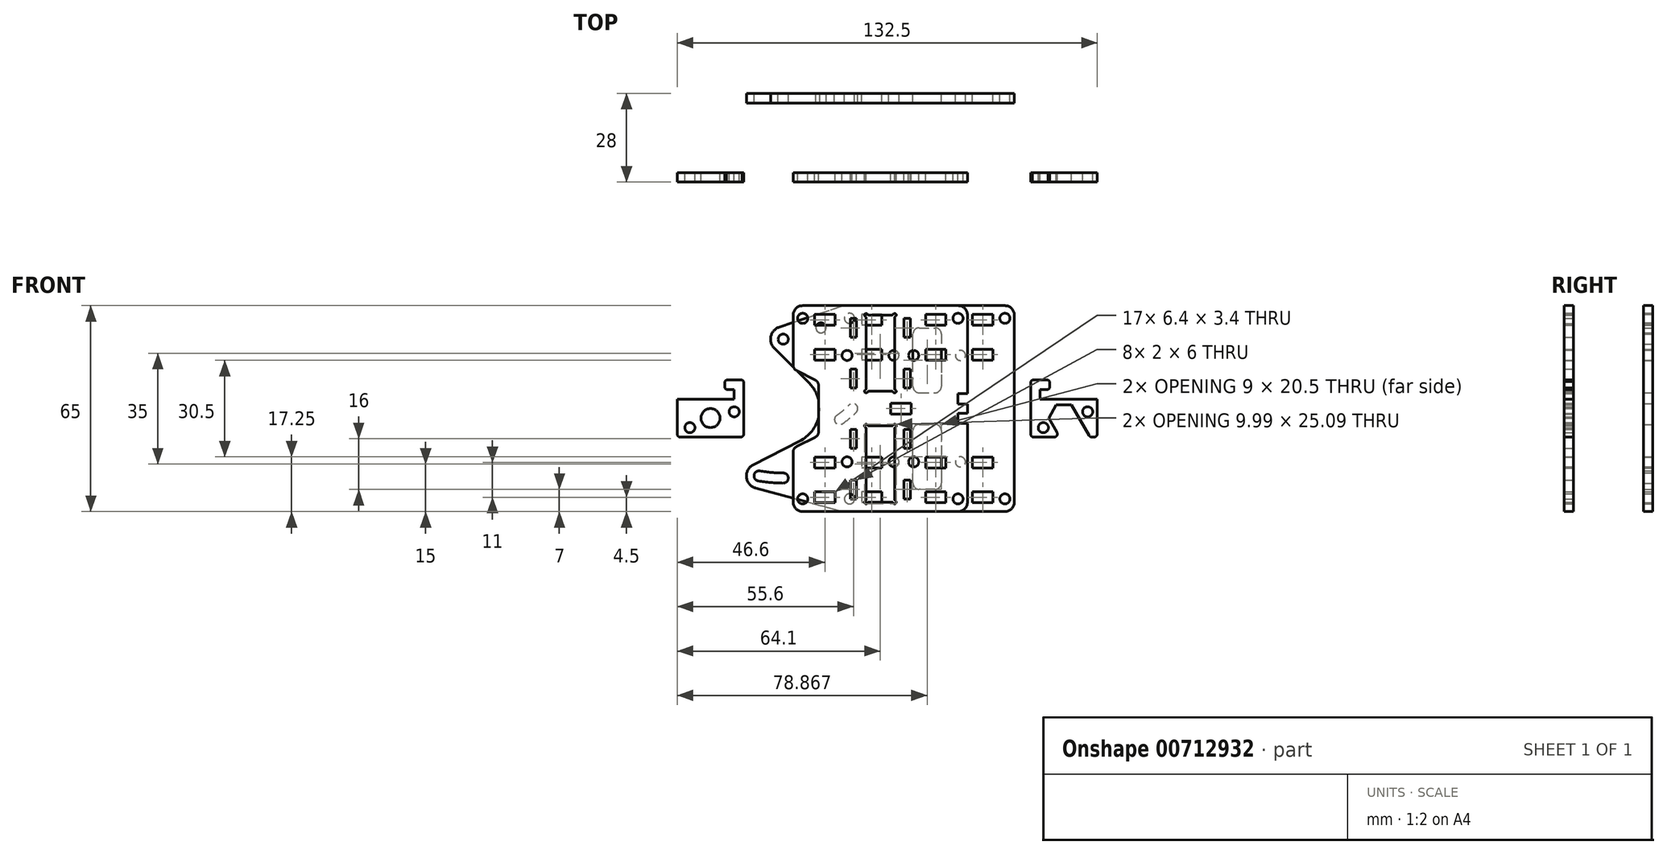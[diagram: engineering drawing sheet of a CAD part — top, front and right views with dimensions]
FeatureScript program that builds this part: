
annotation { "Feature Type Name" : "Feature", "Feature Type Description" : "" }
export const myFeature = defineFeature(function(context is Context, id is Id, definition is map)
    precondition{}
    {
        {
            var Q0;
            Q0=qCreatedBy(makeId("Front.planeOp"),FACE);
            var sketch = newSketch(context, id + "F0", { "sketchPlane" : qUnion([Q0])});
            skLineSegment(sketch, "E0", {"start": v(-7.5, 12.5) * mm, "end": v(-9.5, 12.5) * mm});
            skLineSegment(sketch, "E1", {"start": v(9.5, 12.5) * mm, "end": v(7.5, 12.5) * mm});
            skLineSegment(sketch, "E2", {"start": v(-9.5, -12.5) * mm, "end": v(-7.5, -12.5) * mm});
            skLineSegment(sketch, "E3", {"start": v(7.5, -12.5) * mm, "end": v(9.5, -12.5) * mm});
            skLineSegment(sketch, "E4", {"start": v(-7.5, -22.5) * mm, "end": v(-9.5, -22.5) * mm});
            skLineSegment(sketch, "E5", {"start": v(9.5, -22.5) * mm, "end": v(7.5, -22.5) * mm});
            skLineSegment(sketch, "E6", {"start": v(-9.5, 22.5) * mm, "end": v(-7.5, 22.5) * mm});
            skLineSegment(sketch, "E7", {"start": v(7.5, 22.5) * mm, "end": v(9.5, 22.5) * mm});
            skLineSegment(sketch, "E8", {"start": v(27.5, 1.5) * mm, "end": v(27.5, -1.5) * mm});
            skArc(sketch, "E9", {"start": v(4.75, 29.12) * mm, "mid": v(4.85, 29.9) * mm, "end": v(4.07, 29.8) * mm});
            skArc(sketch, "E10", {"start": v(3.63, 29.55) * mm, "mid": v(3.88, 29.62) * mm, "end": v(4.07, 29.8) * mm});
            skArc(sketch, "E11", {"start": v(4.75, 29.12) * mm, "mid": v(4.57, 28.93) * mm, "end": v(4.5, 28.68) * mm});
            skLineSegment(sketch, "E12", {"start": v(4.5, 6.32) * mm, "end": v(4.5, 28.68) * mm});
            skArc(sketch, "E13", {"start": v(4.5, 6.32) * mm, "mid": v(4.57, 6.07) * mm, "end": v(4.75, 5.88) * mm});
            skArc(sketch, "E14", {"start": v(4.07, 5.2) * mm, "mid": v(4.85, 5.1) * mm, "end": v(4.75, 5.88) * mm});
            skArc(sketch, "E15", {"start": v(4.07, 5.2) * mm, "mid": v(3.88, 5.38) * mm, "end": v(3.63, 5.45) * mm});
            skLineSegment(sketch, "E16", {"start": v(-3.63, 5.45) * mm, "end": v(3.63, 5.45) * mm});
            skArc(sketch, "E17", {"start": v(-3.63, 5.45) * mm, "mid": v(-3.88, 5.38) * mm, "end": v(-4.07, 5.2) * mm});
            skArc(sketch, "E18", {"start": v(-4.75, 5.88) * mm, "mid": v(-4.85, 5.1) * mm, "end": v(-4.07, 5.2) * mm});
            skArc(sketch, "E19", {"start": v(-4.75, 5.88) * mm, "mid": v(-4.57, 6.07) * mm, "end": v(-4.5, 6.32) * mm});
            skLineSegment(sketch, "E20", {"start": v(-4.5, 28.68) * mm, "end": v(-4.5, 6.32) * mm});
            skArc(sketch, "E21", {"start": v(-4.5, 28.68) * mm, "mid": v(-4.57, 28.93) * mm, "end": v(-4.75, 29.12) * mm});
            skArc(sketch, "E22", {"start": v(-4.07, 29.8) * mm, "mid": v(-4.85, 29.9) * mm, "end": v(-4.75, 29.12) * mm});
            skArc(sketch, "E23", {"start": v(-4.07, 29.8) * mm, "mid": v(-3.88, 29.62) * mm, "end": v(-3.63, 29.55) * mm});
            skLineSegment(sketch, "E24", {"start": v(3.63, 29.55) * mm, "end": v(-3.63, 29.55) * mm});
            skArc(sketch, "E25", {"start": v(4.75, -5.88) * mm, "mid": v(4.85, -5.1) * mm, "end": v(4.07, -5.2) * mm});
            skArc(sketch, "E26", {"start": v(3.63, -5.45) * mm, "mid": v(3.88, -5.38) * mm, "end": v(4.07, -5.2) * mm});
            skArc(sketch, "E27", {"start": v(4.75, -5.88) * mm, "mid": v(4.57, -6.07) * mm, "end": v(4.5, -6.32) * mm});
            skLineSegment(sketch, "E28", {"start": v(4.5, -28.68) * mm, "end": v(4.5, -6.32) * mm});
            skArc(sketch, "E29", {"start": v(4.5, -28.68) * mm, "mid": v(4.57, -28.93) * mm, "end": v(4.75, -29.12) * mm});
            skArc(sketch, "E30", {"start": v(4.07, -29.8) * mm, "mid": v(4.85, -29.9) * mm, "end": v(4.75, -29.12) * mm});
            skArc(sketch, "E31", {"start": v(4.07, -29.8) * mm, "mid": v(3.88, -29.62) * mm, "end": v(3.63, -29.55) * mm});
            skLineSegment(sketch, "E32", {"start": v(-3.63, -29.55) * mm, "end": v(3.63, -29.55) * mm});
            skArc(sketch, "E33", {"start": v(-3.63, -29.55) * mm, "mid": v(-3.88, -29.62) * mm, "end": v(-4.07, -29.8) * mm});
            skArc(sketch, "E34", {"start": v(-4.75, -29.12) * mm, "mid": v(-4.85, -29.9) * mm, "end": v(-4.07, -29.8) * mm});
            skArc(sketch, "E35", {"start": v(-4.75, -29.12) * mm, "mid": v(-4.57, -28.93) * mm, "end": v(-4.5, -28.68) * mm});
            skLineSegment(sketch, "E36", {"start": v(-4.5, -6.32) * mm, "end": v(-4.5, -28.68) * mm});
            skArc(sketch, "E37", {"start": v(-4.5, -6.32) * mm, "mid": v(-4.57, -6.07) * mm, "end": v(-4.75, -5.88) * mm});
            skArc(sketch, "E38", {"start": v(-4.07, -5.2) * mm, "mid": v(-4.85, -5.1) * mm, "end": v(-4.75, -5.88) * mm});
            skArc(sketch, "E39", {"start": v(-4.07, -5.2) * mm, "mid": v(-3.88, -5.38) * mm, "end": v(-3.63, -5.45) * mm});
            skLineSegment(sketch, "E40", {"start": v(3.63, -5.45) * mm, "end": v(-3.63, -5.45) * mm});
            skLineSegment(sketch, "E41", {"start": v(24.4, 1.5) * mm, "end": v(27.5, 1.5) * mm});
            skLineSegment(sketch, "E42", {"start": v(27.5, -1.5) * mm, "end": v(24.4, -1.5) * mm});
            skLineSegment(sketch, "E43", {"start": v(27.5, 4.7) * mm, "end": v(24.4, 4.7) * mm});
            skLineSegment(sketch, "E44", {"start": v(24.4, 4.7) * mm, "end": v(24.4, 1.5) * mm});
            skLineSegment(sketch, "E45", {"start": v(24.4, -4.7) * mm, "end": v(27.5, -4.7) * mm});
            skLineSegment(sketch, "E46", {"start": v(24.4, -1.5) * mm, "end": v(24.4, -4.7) * mm});
            skLineSegment(sketch, "E47", {"start": v(9.7, -1.7) * mm, "end": v(9.7, 1.7) * mm});
            skLineSegment(sketch, "E48", {"start": v(9.7, 1.7) * mm, "end": v(3.3, 1.7) * mm});
            skLineSegment(sketch, "E49", {"start": v(9.7, -1.7) * mm, "end": v(3.3, -1.7) * mm});
            skLineSegment(sketch, "E50", {"start": v(3.3, 1.7) * mm, "end": v(3.3, -1.7) * mm});
            skLineSegment(sketch, "E51", {"start": v(9.5, 28.5) * mm, "end": v(7.5, 28.5) * mm});
            skLineSegment(sketch, "E52", {"start": v(7.5, 6.5) * mm, "end": v(9.5, 6.5) * mm});
            skLineSegment(sketch, "E53", {"start": v(9.5, -6.5) * mm, "end": v(7.5, -6.5) * mm});
            skLineSegment(sketch, "E54", {"start": v(7.5, -28.5) * mm, "end": v(9.5, -28.5) * mm});
            skLineSegment(sketch, "E55", {"start": v(-7.5, 28.5) * mm, "end": v(-9.5, 28.5) * mm});
            skLineSegment(sketch, "E56", {"start": v(-9.5, 6.5) * mm, "end": v(-7.5, 6.5) * mm});
            skLineSegment(sketch, "E57", {"start": v(-7.5, -6.5) * mm, "end": v(-9.5, -6.5) * mm});
            skLineSegment(sketch, "E58", {"start": v(-9.5, -28.5) * mm, "end": v(-7.5, -28.5) * mm});
            skLineSegment(sketch, "E59", {"start": v(9.5, 22.5) * mm, "end": v(9.5, 28.5) * mm});
            skLineSegment(sketch, "E60", {"start": v(7.5, 28.5) * mm, "end": v(7.5, 22.5) * mm});
            skLineSegment(sketch, "E61", {"start": v(9.5, 6.5) * mm, "end": v(9.5, 12.5) * mm});
            skLineSegment(sketch, "E62", {"start": v(7.5, 12.5) * mm, "end": v(7.5, 6.5) * mm});
            skLineSegment(sketch, "E63", {"start": v(9.5, -12.5) * mm, "end": v(9.5, -6.5) * mm});
            skLineSegment(sketch, "E64", {"start": v(7.5, -6.5) * mm, "end": v(7.5, -12.5) * mm});
            skLineSegment(sketch, "E65", {"start": v(9.5, -28.5) * mm, "end": v(9.5, -22.5) * mm});
            skLineSegment(sketch, "E66", {"start": v(7.5, -22.5) * mm, "end": v(7.5, -28.5) * mm});
            skLineSegment(sketch, "E67", {"start": v(-7.5, 22.5) * mm, "end": v(-7.5, 28.5) * mm});
            skLineSegment(sketch, "E68", {"start": v(-9.5, 28.5) * mm, "end": v(-9.5, 22.5) * mm});
            skLineSegment(sketch, "E69", {"start": v(-7.5, 6.5) * mm, "end": v(-7.5, 12.5) * mm});
            skLineSegment(sketch, "E70", {"start": v(-9.5, 12.5) * mm, "end": v(-9.5, 6.5) * mm});
            skLineSegment(sketch, "E71", {"start": v(-7.5, -12.5) * mm, "end": v(-7.5, -6.5) * mm});
            skLineSegment(sketch, "E72", {"start": v(-9.5, -6.5) * mm, "end": v(-9.5, -12.5) * mm});
            skLineSegment(sketch, "E73", {"start": v(-7.5, -28.5) * mm, "end": v(-7.5, -22.5) * mm});
            skLineSegment(sketch, "E74", {"start": v(-9.5, -22.5) * mm, "end": v(-9.5, -28.5) * mm});
            skLineSegment(sketch, "E75", {"start": v(-14.3, 26.3) * mm, "end": v(-14.3, 29.7) * mm});
            skLineSegment(sketch, "E76", {"start": v(-14.3, 29.7) * mm, "end": v(-20.7, 29.7) * mm});
            skLineSegment(sketch, "E77", {"start": v(-14.3, 26.3) * mm, "end": v(-20.7, 26.3) * mm});
            skLineSegment(sketch, "E78", {"start": v(-20.7, 29.7) * mm, "end": v(-20.7, 26.3) * mm});
            skLineSegment(sketch, "E79", {"start": v(-14.3, 15.3) * mm, "end": v(-14.3, 18.7) * mm});
            skLineSegment(sketch, "E80", {"start": v(-14.3, 18.7) * mm, "end": v(-20.7, 18.7) * mm});
            skLineSegment(sketch, "E81", {"start": v(-14.3, 15.3) * mm, "end": v(-20.7, 15.3) * mm});
            skLineSegment(sketch, "E82", {"start": v(-20.7, 18.7) * mm, "end": v(-20.7, 15.3) * mm});
            skLineSegment(sketch, "E83", {"start": v(-14.3, -18.7) * mm, "end": v(-14.3, -15.3) * mm});
            skLineSegment(sketch, "E84", {"start": v(-14.3, -15.3) * mm, "end": v(-20.7, -15.3) * mm});
            skLineSegment(sketch, "E85", {"start": v(-14.3, -18.7) * mm, "end": v(-20.7, -18.7) * mm});
            skLineSegment(sketch, "E86", {"start": v(-20.7, -15.3) * mm, "end": v(-20.7, -18.7) * mm});
            skLineSegment(sketch, "E87", {"start": v(-14.3, -29.7) * mm, "end": v(-14.3, -26.3) * mm});
            skLineSegment(sketch, "E88", {"start": v(-14.3, -26.3) * mm, "end": v(-20.7, -26.3) * mm});
            skLineSegment(sketch, "E89", {"start": v(-14.3, -29.7) * mm, "end": v(-20.7, -29.7) * mm});
            skLineSegment(sketch, "E90", {"start": v(-20.7, -26.3) * mm, "end": v(-20.7, -29.7) * mm});
            skCircle(sketch, "E91", {"center": v(-24.5, 28.5) * mm, "radius": 1.6 * mm});
            skCircle(sketch, "E92", {"center": v(-24.5, -28.5) * mm, "radius": 1.6 * mm});
            skLineSegment(sketch, "E93", {"start": v(20.7, 26.3) * mm, "end": v(20.7, 29.7) * mm});
            skLineSegment(sketch, "E94", {"start": v(20.7, 29.7) * mm, "end": v(14.3, 29.7) * mm});
            skLineSegment(sketch, "E95", {"start": v(20.7, 26.3) * mm, "end": v(14.3, 26.3) * mm});
            skLineSegment(sketch, "E96", {"start": v(14.3, 29.7) * mm, "end": v(14.3, 26.3) * mm});
            skLineSegment(sketch, "E97", {"start": v(20.7, 15.3) * mm, "end": v(20.7, 18.7) * mm});
            skLineSegment(sketch, "E98", {"start": v(20.7, 18.7) * mm, "end": v(14.3, 18.7) * mm});
            skLineSegment(sketch, "E99", {"start": v(20.7, 15.3) * mm, "end": v(14.3, 15.3) * mm});
            skLineSegment(sketch, "E100", {"start": v(14.3, 18.7) * mm, "end": v(14.3, 15.3) * mm});
            skLineSegment(sketch, "E101", {"start": v(20.7, -18.7) * mm, "end": v(20.7, -15.3) * mm});
            skLineSegment(sketch, "E102", {"start": v(20.7, -15.3) * mm, "end": v(14.3, -15.3) * mm});
            skLineSegment(sketch, "E103", {"start": v(20.7, -18.7) * mm, "end": v(14.3, -18.7) * mm});
            skLineSegment(sketch, "E104", {"start": v(14.3, -15.3) * mm, "end": v(14.3, -18.7) * mm});
            skLineSegment(sketch, "E105", {"start": v(20.7, -29.7) * mm, "end": v(20.7, -26.3) * mm});
            skLineSegment(sketch, "E106", {"start": v(20.7, -26.3) * mm, "end": v(14.3, -26.3) * mm});
            skLineSegment(sketch, "E107", {"start": v(20.7, -29.7) * mm, "end": v(14.3, -29.7) * mm});
            skLineSegment(sketch, "E108", {"start": v(14.3, -26.3) * mm, "end": v(14.3, -29.7) * mm});
            skCircle(sketch, "E109", {"center": v(24.5, 28.5) * mm, "radius": 1.6 * mm});
            skCircle(sketch, "E110", {"center": v(24.5, -28.5) * mm, "radius": 1.6 * mm});
            skLineSegment(sketch, "E111", {"start": v(27.5, -4.7) * mm, "end": v(27.5, -29.5) * mm});
            skArc(sketch, "E112", {"start": v(24.5, -32.5) * mm, "mid": v(26.62, -31.62) * mm, "end": v(27.5, -29.5) * mm});
            skArc(sketch, "E113", {"start": v(27.5, 29.5) * mm, "mid": v(26.62, 31.62) * mm, "end": v(24.5, 32.5) * mm});
            skCircle(sketch, "E114", {"center": v(-10.5, 16.8) * mm, "radius": 1.6 * mm});
            skCircle(sketch, "E115", {"center": v(10.5, 16.8) * mm, "radius": 1.6 * mm});
            skCircle(sketch, "E116", {"center": v(10.5, -16.8) * mm, "radius": 1.6 * mm});
            skCircle(sketch, "E117", {"center": v(-10.5, -16.8) * mm, "radius": 1.6 * mm});
            skLineSegment(sketch, "E118", {"start": v(-24.5, 32.5) * mm, "end": v(24.5, 32.5) * mm});
            skLineSegment(sketch, "E119", {"start": v(24.5, -32.5) * mm, "end": v(-24.5, -32.5) * mm});
            skArc(sketch, "E120", {"start": v(-27.5, 13.74) * mm, "mid": v(-27.2, 12.68) * mm, "end": v(-26.4, 11.95) * mm});
            skLineSegment(sketch, "E121", {"start": v(-26.4, 11.95) * mm, "end": v(-20.6, 9.05) * mm});
            skArc(sketch, "E122", {"start": v(-19.5, 7.26) * mm, "mid": v(-19.8, 8.32) * mm, "end": v(-20.6, 9.05) * mm});
            skLineSegment(sketch, "E123", {"start": v(-19.5, 7.26) * mm, "end": v(-19.5, -7.26) * mm});
            skArc(sketch, "E124", {"start": v(-20.6, -9.05) * mm, "mid": v(-19.8, -8.32) * mm, "end": v(-19.5, -7.26) * mm});
            skLineSegment(sketch, "E125", {"start": v(-20.6, -9.05) * mm, "end": v(-26.4, -11.95) * mm});
            skArc(sketch, "E126", {"start": v(-26.4, -11.95) * mm, "mid": v(-27.2, -12.68) * mm, "end": v(-27.5, -13.74) * mm});
            skLineSegment(sketch, "E127", {"start": v(-27.5, 29.5) * mm, "end": v(-27.5, 13.74) * mm});
            skArc(sketch, "E128", {"start": v(-24.5, 32.5) * mm, "mid": v(-26.62, 31.62) * mm, "end": v(-27.5, 29.5) * mm});
            skLineSegment(sketch, "E129", {"start": v(-27.5, -13.74) * mm, "end": v(-27.5, -29.5) * mm});
            skArc(sketch, "E130", {"start": v(-27.5, -29.5) * mm, "mid": v(-26.62, -31.62) * mm, "end": v(-24.5, -32.5) * mm});
            skLineSegment(sketch, "E131", {"start": v(27.5, 29.5) * mm, "end": v(27.5, 4.7) * mm});
            skSolve(sketch);
        }
        {
            var Q0;
            Q0=makeQuery(id+"F0.imprint","IMPRINT",FACE,{"disambiguationData":[TD([[makeQuery(id+"F0.imprint","IMPRINT",EDGE,{"derivedFrom":sQuery(id+"F0.wireOp",EDGE,"E0")}),-1.0]])]});
            extrude(context, id + "F1", {"entities" : qUnion([Q0]), "depth" : 3 * mm, "offsetDistance" : 25 * mm});
        }
        {
            var Q0;
            Q0=qCreatedBy(makeId("Front.planeOp"),FACE);
            cPlane(context, id + "F2", {"entities" : qUnion([Q0]), "cplaneType" : CPlaneType.OFFSET, "offset" : 25 * mm, "oppositeDirection" : true, "width" : 150 * mm, "height" : 150 * mm});
        }
        {
            var Q0;
            Q0=qCreatedBy(id+"F2.planeOp",FACE);
            var sketch = newSketch(context, id + "F3", { "sketchPlane" : qUnion([Q0])});
            skArc(sketch, "E132", {"start": v(19.27, 23.5) * mm, "mid": v(18.68, 24.91) * mm, "end": v(17.27, 25.5) * mm});
            skLineSegment(sketch, "E133", {"start": v(12.27, 25.5) * mm, "end": v(17.27, 25.5) * mm});
            skArc(sketch, "E134", {"start": v(12.27, 25.5) * mm, "mid": v(10.85, 24.91) * mm, "end": v(10.27, 23.5) * mm});
            skArc(sketch, "E135", {"start": v(17.27, -25.5) * mm, "mid": v(18.68, -24.91) * mm, "end": v(19.27, -23.5) * mm});
            skLineSegment(sketch, "E136", {"start": v(17.27, -25.5) * mm, "end": v(12.27, -25.5) * mm});
            skArc(sketch, "E137", {"start": v(10.27, -23.5) * mm, "mid": v(10.85, -24.91) * mm, "end": v(12.27, -25.5) * mm});
            skLineSegment(sketch, "E138", {"start": v(10.27, 7) * mm, "end": v(10.27, 23.5) * mm});
            skArc(sketch, "E139", {"start": v(10.27, 7) * mm, "mid": v(10.85, 5.59) * mm, "end": v(12.27, 5) * mm});
            skLineSegment(sketch, "E140", {"start": v(19.27, 23.5) * mm, "end": v(19.27, 7) * mm});
            skLineSegment(sketch, "E141", {"start": v(12.27, 5) * mm, "end": v(17.27, 5) * mm});
            skArc(sketch, "E142", {"start": v(17.27, 5) * mm, "mid": v(18.68, 5.59) * mm, "end": v(19.27, 7) * mm});
            skLineSegment(sketch, "E143", {"start": v(10.27, -23.5) * mm, "end": v(10.27, -7) * mm});
            skArc(sketch, "E144", {"start": v(12.27, -5) * mm, "mid": v(10.85, -5.59) * mm, "end": v(10.27, -7) * mm});
            skLineSegment(sketch, "E145", {"start": v(12.27, -5) * mm, "end": v(17.27, -5) * mm});
            skLineSegment(sketch, "E146", {"start": v(19.27, -7) * mm, "end": v(19.27, -23.5) * mm});
            skArc(sketch, "E147", {"start": v(19.27, -7) * mm, "mid": v(18.68, -5.59) * mm, "end": v(17.27, -5) * mm});
            skCircle(sketch, "E148", {"center": v(-9.73, 28.5) * mm, "radius": 1.6 * mm});
            skCircle(sketch, "E149", {"center": v(-9.73, -28.5) * mm, "radius": 1.6 * mm});
            skLineSegment(sketch, "E150", {"start": v(0.47, 26.3) * mm, "end": v(0.47, 29.7) * mm});
            skLineSegment(sketch, "E151", {"start": v(0.47, 29.7) * mm, "end": v(-5.93, 29.7) * mm});
            skLineSegment(sketch, "E152", {"start": v(0.47, 26.3) * mm, "end": v(-5.93, 26.3) * mm});
            skLineSegment(sketch, "E153", {"start": v(-5.93, 29.7) * mm, "end": v(-5.93, 26.3) * mm});
            skLineSegment(sketch, "E154", {"start": v(0.47, 15.3) * mm, "end": v(0.47, 18.7) * mm});
            skLineSegment(sketch, "E155", {"start": v(0.47, 18.7) * mm, "end": v(-5.93, 18.7) * mm});
            skLineSegment(sketch, "E156", {"start": v(0.47, 15.3) * mm, "end": v(-5.93, 15.3) * mm});
            skLineSegment(sketch, "E157", {"start": v(-5.93, 18.7) * mm, "end": v(-5.93, 15.3) * mm});
            skLineSegment(sketch, "E158", {"start": v(0.47, -18.7) * mm, "end": v(0.47, -15.3) * mm});
            skLineSegment(sketch, "E159", {"start": v(0.47, -15.3) * mm, "end": v(-5.93, -15.3) * mm});
            skLineSegment(sketch, "E160", {"start": v(0.47, -18.7) * mm, "end": v(-5.93, -18.7) * mm});
            skLineSegment(sketch, "E161", {"start": v(-5.93, -15.3) * mm, "end": v(-5.93, -18.7) * mm});
            skLineSegment(sketch, "E162", {"start": v(0.47, -29.7) * mm, "end": v(0.47, -26.3) * mm});
            skLineSegment(sketch, "E163", {"start": v(0.47, -26.3) * mm, "end": v(-5.93, -26.3) * mm});
            skLineSegment(sketch, "E164", {"start": v(0.47, -29.7) * mm, "end": v(-5.93, -29.7) * mm});
            skLineSegment(sketch, "E165", {"start": v(-5.93, -26.3) * mm, "end": v(-5.93, -29.7) * mm});
            skCircle(sketch, "E166", {"center": v(-30.65, 21.92) * mm, "radius": 1.6 * mm});
            skArc(sketch, "E167", {"start": v(-7.6, -1.13) * mm, "mid": v(-7.6, 1.13) * mm, "end": v(-9.86, 1.13) * mm});
            skArc(sketch, "E168", {"start": v(-13.8, -2.16) * mm, "mid": v(-11.76, -0.6) * mm, "end": v(-9.86, 1.13) * mm});
            skArc(sketch, "E169", {"start": v(-11.96, -4.78) * mm, "mid": v(-9.7, -3.05) * mm, "end": v(-7.6, -1.13) * mm});
            skArc(sketch, "E170", {"start": v(-13.8, -2.16) * mm, "mid": v(-14.18, -4.4) * mm, "end": v(-11.96, -4.78) * mm});
            skArc(sketch, "E171", {"start": v(-37.99, -19.68) * mm, "mid": v(-34.34, -20.16) * mm, "end": v(-30.65, -20.32) * mm});
            skArc(sketch, "E172", {"start": v(-30.65, -23.52) * mm, "mid": v(-29.05, -21.92) * mm, "end": v(-30.65, -20.32) * mm});
            skArc(sketch, "E173", {"start": v(-38.54, -22.83) * mm, "mid": v(-34.61, -23.35) * mm, "end": v(-30.65, -23.52) * mm});
            skArc(sketch, "E174", {"start": v(-37.99, -19.68) * mm, "mid": v(-39.84, -20.98) * mm, "end": v(-38.54, -22.83) * mm});
            skCircle(sketch, "E175", {"center": v(-18.73, 25.5) * mm, "radius": 1.6 * mm});
            skLineSegment(sketch, "E176", {"start": v(-33.48, 19.1) * mm, "end": v(-22.52, 8.13) * mm});
            skLineSegment(sketch, "E177", {"start": v(-40.08, -17.69) * mm, "end": v(-25.44, -10.25) * mm});
            skArc(sketch, "E178", {"start": v(-31.93, 25.71) * mm, "mid": v(-34.55, 22.83) * mm, "end": v(-33.48, 19.1) * mm});
            skArc(sketch, "E179", {"start": v(-40.08, -17.69) * mm, "mid": v(-42.24, -21.67) * mm, "end": v(-39.3, -25.12) * mm});
            skArc(sketch, "E180", {"start": v(-25.44, -10.25) * mm, "mid": v(-19.3, -1.8) * mm, "end": v(-22.52, 8.13) * mm});
            skLineSegment(sketch, "E181", {"start": v(-39.3, -25.12) * mm, "end": v(-12.24, -32.36) * mm});
            skArc(sketch, "E182", {"start": v(-12.24, -32.36) * mm, "mid": v(-11.73, -32.47) * mm, "end": v(-11.2, -32.5) * mm});
            skLineSegment(sketch, "E183", {"start": v(-31.93, 25.71) * mm, "end": v(-12.35, 32.3) * mm});
            skArc(sketch, "E184", {"start": v(-11.08, 32.5) * mm, "mid": v(-11.72, 32.45) * mm, "end": v(-12.35, 32.3) * mm});
            skCircle(sketch, "E185", {"center": v(39.27, 28.5) * mm, "radius": 1.6 * mm});
            skCircle(sketch, "E186", {"center": v(39.27, -28.5) * mm, "radius": 1.6 * mm});
            skLineSegment(sketch, "E187", {"start": v(35.47, 26.3) * mm, "end": v(35.47, 29.7) * mm});
            skLineSegment(sketch, "E188", {"start": v(35.47, 29.7) * mm, "end": v(29.07, 29.7) * mm});
            skLineSegment(sketch, "E189", {"start": v(35.47, 26.3) * mm, "end": v(29.07, 26.3) * mm});
            skLineSegment(sketch, "E190", {"start": v(29.07, 29.7) * mm, "end": v(29.07, 26.3) * mm});
            skLineSegment(sketch, "E191", {"start": v(35.47, 15.3) * mm, "end": v(35.47, 18.7) * mm});
            skLineSegment(sketch, "E192", {"start": v(35.47, 18.7) * mm, "end": v(29.07, 18.7) * mm});
            skLineSegment(sketch, "E193", {"start": v(35.47, 15.3) * mm, "end": v(29.07, 15.3) * mm});
            skLineSegment(sketch, "E194", {"start": v(29.07, 18.7) * mm, "end": v(29.07, 15.3) * mm});
            skLineSegment(sketch, "E195", {"start": v(35.47, -18.7) * mm, "end": v(35.47, -15.3) * mm});
            skLineSegment(sketch, "E196", {"start": v(35.47, -15.3) * mm, "end": v(29.07, -15.3) * mm});
            skLineSegment(sketch, "E197", {"start": v(35.47, -18.7) * mm, "end": v(29.07, -18.7) * mm});
            skLineSegment(sketch, "E198", {"start": v(29.07, -15.3) * mm, "end": v(29.07, -18.7) * mm});
            skLineSegment(sketch, "E199", {"start": v(35.47, -29.7) * mm, "end": v(35.47, -26.3) * mm});
            skLineSegment(sketch, "E200", {"start": v(35.47, -26.3) * mm, "end": v(29.07, -26.3) * mm});
            skLineSegment(sketch, "E201", {"start": v(35.47, -29.7) * mm, "end": v(29.07, -29.7) * mm});
            skLineSegment(sketch, "E202", {"start": v(29.07, -26.3) * mm, "end": v(29.07, -29.7) * mm});
            skLineSegment(sketch, "E203", {"start": v(-11.08, 32.5) * mm, "end": v(39.27, 32.5) * mm});
            skArc(sketch, "E204", {"start": v(42.27, 29.5) * mm, "mid": v(41.39, 31.62) * mm, "end": v(39.27, 32.5) * mm});
            skLineSegment(sketch, "E205", {"start": v(39.27, -32.5) * mm, "end": v(-11.2, -32.5) * mm});
            skLineSegment(sketch, "E206", {"start": v(42.27, 29.5) * mm, "end": v(42.27, -29.5) * mm});
            skArc(sketch, "E207", {"start": v(39.27, -32.5) * mm, "mid": v(41.39, -31.62) * mm, "end": v(42.27, -29.5) * mm});
            skCircle(sketch, "E208", {"center": v(25.27, 16.8) * mm, "radius": 1.6 * mm});
            skCircle(sketch, "E209", {"center": v(4.27, 16.8) * mm, "radius": 1.6 * mm});
            skCircle(sketch, "E210", {"center": v(4.27, -16.8) * mm, "radius": 1.6 * mm});
            skCircle(sketch, "E211", {"center": v(25.27, -16.8) * mm, "radius": 1.6 * mm});
            skSolve(sketch);
        }
        {
            var Q0;
            Q0=makeQuery(id+"F3.imprint","IMPRINT",FACE,{"disambiguationData":[TD([[makeQuery(id+"F3.imprint","IMPRINT",EDGE,{"derivedFrom":sQuery(id+"F3.wireOp",EDGE,"E132")}),-1.0]])]});
            extrude(context, id + "F4", {"entities" : qUnion([Q0]), "depth" : 3 * mm, "offsetDistance" : 25 * mm});
        }
        {
            var Q0;
            Q0=makeQuery(id+"F1.opExtrude","CAP_EDGE",EDGE,{"disambiguationData":[OSD([sQuery(id+"F0.wireOp",EDGE,"E20")])],"isStart":true});
            cPoint(context, id + "F5", {"entities" : qUnion([Q0]), "parameter" : 0.5});
        }
        {
            var Q0;
            Q0 = qCreatedBy(id + "F5" ,VERTEX);
            var Q1;
            Q1=makeQuery(id+"F1.opExtrude","CAP_EDGE",EDGE,{"disambiguationData":[OSD([sQuery(id+"F0.wireOp",EDGE,"E20")])],"isStart":true});
            cPlane(context, id + "F6", {"entities" : qUnion([Q0, Q1]), "cplaneType" : CPlaneType.LINE_POINT, "offset" : 25 * mm, "width" : 150 * mm, "height" : 150 * mm});
        }
        {
            var Q0;
            Q0=qCreatedBy(id+"F6.planeOp",FACE);
            var sketch = newSketch(context, id + "F7", { "sketchPlane" : qUnion([Q0])});
            skCircle(sketch, "E212", {"center": v(0, 9) * mm, "radius": 7.5 * mm, "construction": true});
            skSolve(sketch);
        }
        {
            var Q0;
            Q0=makeQuery(id+"F1.opExtrude","CAP_EDGE",EDGE,{"disambiguationData":[OSD([sQuery(id+"F0.wireOp",EDGE,"E36")])],"isStart":true});
            cPoint(context, id + "F8", {"entities" : qUnion([Q0]), "parameter" : 0.5});
        }
        {
            var Q0;
            Q0 = qCreatedBy(id + "F8" ,VERTEX);
            var Q1;
            Q1=makeQuery(id+"F1.opExtrude","CAP_EDGE",EDGE,{"disambiguationData":[OSD([sQuery(id+"F0.wireOp",EDGE,"E36")])],"isStart":true});
            cPlane(context, id + "F9", {"entities" : qUnion([Q0, Q1]), "cplaneType" : CPlaneType.LINE_POINT, "offset" : 25 * mm, "width" : 150 * mm, "height" : 150 * mm});
        }
        {
            var Q0;
            Q0=qCreatedBy(id+"F9.planeOp",FACE);
            var sketch = newSketch(context, id + "F10", { "sketchPlane" : qUnion([Q0])});
            skCircle(sketch, "E213", {"center": v(0, 9) * mm, "radius": 7.5 * mm, "construction": true});
            skSolve(sketch);
        }
        {
            var Q0;
            Q0=qCreatedBy(makeId("Front.planeOp"),FACE);
            var sketch = newSketch(context, id + "F11", { "sketchPlane" : qUnion([Q0])});
            skLineSegment(sketch, "E214", {"start": v(-46.1, 6) * mm, "end": v(-46.1, 3) * mm});
            skLineSegment(sketch, "E215", {"start": v(-64.1, 3) * mm, "end": v(-46.1, 3) * mm});
            skLineSegment(sketch, "E216", {"start": v(-64.1, 3) * mm, "end": v(-64.1, -8) * mm});
            skArc(sketch, "E217", {"start": v(-64.1, -8) * mm, "mid": v(-63.8, -8.7) * mm, "end": v(-63.1, -9) * mm});
            skLineSegment(sketch, "E218", {"start": v(-63.1, -9) * mm, "end": v(-44.1, -9) * mm});
            skArc(sketch, "E219", {"start": v(-44.1, -9) * mm, "mid": v(-43.4, -8.7) * mm, "end": v(-43.1, -8) * mm});
            skCircle(sketch, "E220", {"center": v(-46.1, -1) * mm, "radius": 1.6 * mm});
            skCircle(sketch, "E221", {"center": v(-60.1, -6) * mm, "radius": 1.6 * mm});
            skCircle(sketch, "E222", {"center": v(-53.6, -3) * mm, "radius": 3 * mm});
            skLineSegment(sketch, "E223", {"start": v(-48.6, 9) * mm, "end": v(-49.1, 8.5) * mm});
            skLineSegment(sketch, "E224", {"start": v(-43.6, 9) * mm, "end": v(-48.6, 9) * mm});
            skLineSegment(sketch, "E225", {"start": v(-43.1, -8) * mm, "end": v(-43.1, 8.5) * mm});
            skLineSegment(sketch, "E226", {"start": v(-43.6, 9) * mm, "end": v(-43.1, 8.5) * mm});
            skLineSegment(sketch, "E227", {"start": v(-49.1, 8.5) * mm, "end": v(-49.1, 6.5) * mm});
            skLineSegment(sketch, "E228", {"start": v(-48.6, 6) * mm, "end": v(-46.1, 6) * mm});
            skLineSegment(sketch, "E229", {"start": v(-49.1, 6.5) * mm, "end": v(-48.6, 6) * mm});
            skLineSegment(sketch, "E230", {"start": v(50.4, 3) * mm, "end": v(50.4, 6) * mm});
            skLineSegment(sketch, "E231", {"start": v(53.1, -3) * mm, "end": v(55.5, 1.16) * mm});
            skLineSegment(sketch, "E232", {"start": v(55.5, 1.16) * mm, "end": v(60.3, 1.16) * mm});
            skLineSegment(sketch, "E233", {"start": v(50.4, 3) * mm, "end": v(68.4, 3) * mm});
            skArc(sketch, "E234", {"start": v(47.4, -8) * mm, "mid": v(47.7, -8.7) * mm, "end": v(48.4, -9) * mm});
            skLineSegment(sketch, "E235", {"start": v(48.4, -9) * mm, "end": v(54.83, -9) * mm});
            skLineSegment(sketch, "E236", {"start": v(53.1, -3) * mm, "end": v(55.7, -7.5) * mm});
            skArc(sketch, "E237", {"start": v(54.83, -9) * mm, "mid": v(55.7, -8.5) * mm, "end": v(55.7, -7.5) * mm});
            skLineSegment(sketch, "E238", {"start": v(60.3, 1.16) * mm, "end": v(65.88, -8.5) * mm});
            skArc(sketch, "E239", {"start": v(65.88, -8.5) * mm, "mid": v(66.24, -8.87) * mm, "end": v(66.74, -9) * mm});
            skLineSegment(sketch, "E240", {"start": v(66.74, -9) * mm, "end": v(67.4, -9) * mm});
            skLineSegment(sketch, "E241", {"start": v(68.4, -8) * mm, "end": v(68.4, 3) * mm});
            skArc(sketch, "E242", {"start": v(67.4, -9) * mm, "mid": v(68.1, -8.7) * mm, "end": v(68.4, -8) * mm});
            skCircle(sketch, "E243", {"center": v(65.4, -1) * mm, "radius": 1.6 * mm});
            skCircle(sketch, "E244", {"center": v(51.4, -6) * mm, "radius": 1.6 * mm});
            skLineSegment(sketch, "E245", {"start": v(53.4, 8.5) * mm, "end": v(52.9, 9) * mm});
            skLineSegment(sketch, "E246", {"start": v(47.9, 9) * mm, "end": v(52.9, 9) * mm});
            skLineSegment(sketch, "E247", {"start": v(47.4, -8) * mm, "end": v(47.4, 8.5) * mm});
            skLineSegment(sketch, "E248", {"start": v(47.9, 9) * mm, "end": v(47.4, 8.5) * mm});
            skLineSegment(sketch, "E249", {"start": v(53.4, 8.5) * mm, "end": v(53.4, 6.5) * mm});
            skLineSegment(sketch, "E250", {"start": v(52.9, 6) * mm, "end": v(50.4, 6) * mm});
            skLineSegment(sketch, "E251", {"start": v(53.4, 6.5) * mm, "end": v(52.9, 6) * mm});
            skSolve(sketch);
        }
        {
            var Q0;
            Q0=makeQuery(id+"F11.imprint","IMPRINT",FACE,{"disambiguationData":[TD([[makeQuery(id+"F11.imprint","IMPRINT",EDGE,{"derivedFrom":sQuery(id+"F11.wireOp",EDGE,"E230")}),1.0]])]});
            var Q1;
            Q1=makeQuery(id+"F11.imprint","IMPRINT",FACE,{"disambiguationData":[TD([[makeQuery(id+"F11.imprint","IMPRINT",EDGE,{"derivedFrom":sQuery(id+"F11.wireOp",EDGE,"E214")}),1.0]])]});
            extrude(context, id + "F12", {"entities" : qUnion([Q0, Q1]), "depth" : 3 * mm, "offsetDistance" : 25 * mm});
        }
    });
